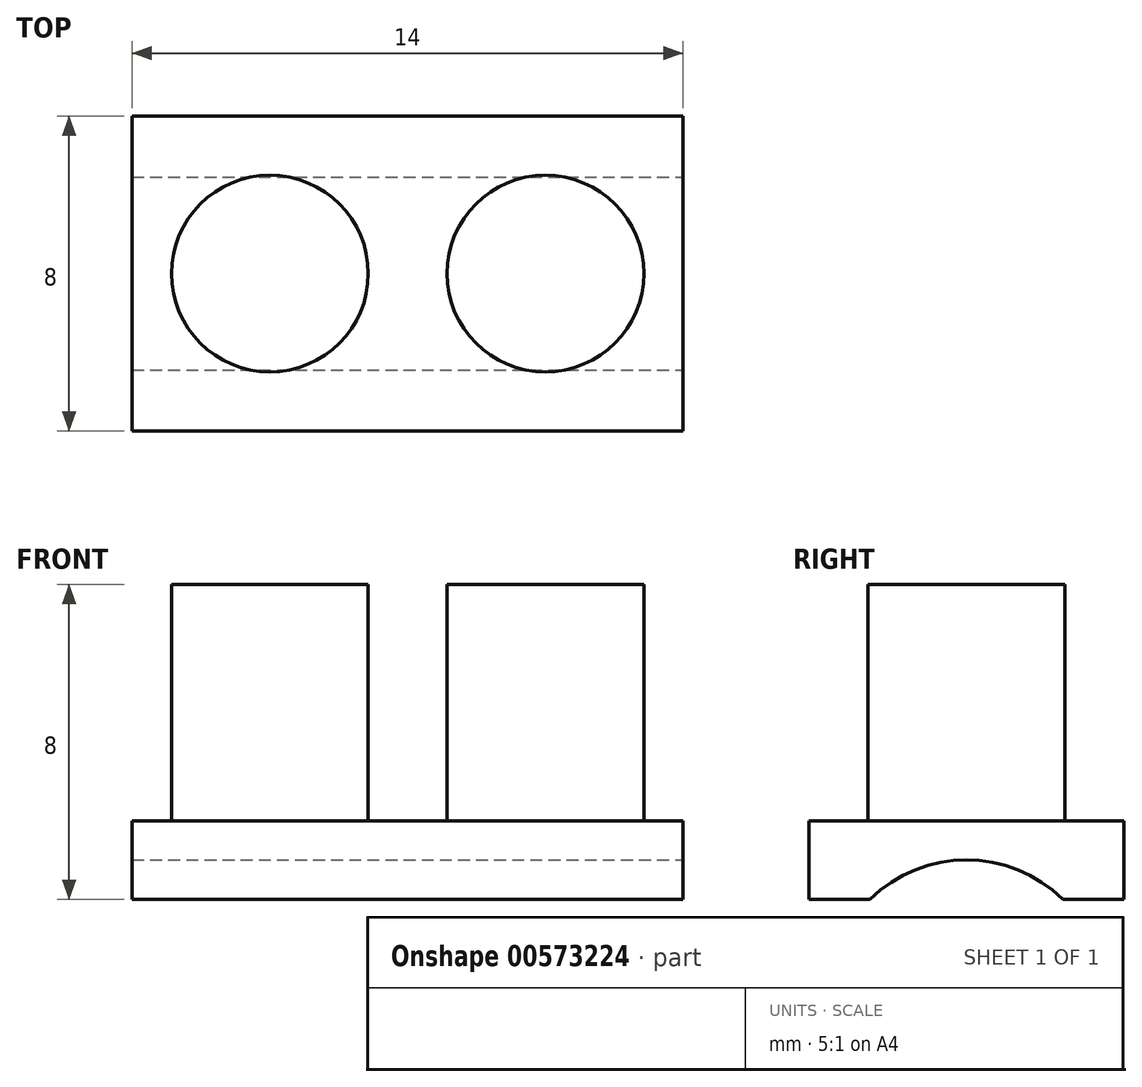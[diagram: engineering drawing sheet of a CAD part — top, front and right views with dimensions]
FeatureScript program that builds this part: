
annotation { "Feature Type Name" : "Feature", "Feature Type Description" : "" }
export const myFeature = defineFeature(function(context is Context, id is Id, definition is map)
    precondition{}
    {
        {
            var Q0;
            Q0=qCreatedBy(makeId("Front.planeOp"),FACE);
            var sketch = newSketch(context, id + "F0", { "sketchPlane" : qUnion([Q0])});
            skLineSegment(sketch, "E0.bottom", {"start": v(-1.14, 0) * mm, "end": v(12.86, 0) * mm});
            skLineSegment(sketch, "E0.top", {"start": v(-1.14, 2) * mm, "end": v(12.86, 2) * mm});
            skLineSegment(sketch, "E0.left", {"start": v(-1.14, 0) * mm, "end": v(-1.14, 2) * mm});
            skLineSegment(sketch, "E0.right", {"start": v(12.86, 0) * mm, "end": v(12.86, 2) * mm});
            skSolve(sketch);
        }
        {
            var Q0;
            Q0=makeQuery(id+"F0.imprint","IMPRINT",FACE,{"disambiguationData":[TD([[makeQuery(id+"F0.imprint","IMPRINT",EDGE,{"derivedFrom":sQuery(id+"F0.wireOp",EDGE,"E0.bottom")}),1.0]])]});
            extrude(context, id + "F1", {"entities" : qUnion([Q0]), "endBound" : BoundingType.SYMMETRIC, "depth" : 8 * mm, "offsetDistance" : 25.4 * mm});
        }
        {
            var Q0;
            Q0=makeQuery(id+"F1.opExtrude","SWEPT_FACE",FACE,{"disambiguationData":[OSD([sQuery(id+"F0.wireOp",EDGE,"E0.top")])]});
            var sketch = newSketch(context, id + "F2", { "sketchPlane" : qUnion([Q0])});
            skCircle(sketch, "E1", {"center": v(2.36, 0) * mm, "radius": 2.5 * mm});
            skCircle(sketch, "E2", {"center": v(9.36, 0) * mm, "radius": 2.5 * mm});
            skSolve(sketch);
        }
        {
            var Q0;
            Q0=makeQuery(id+"F2.imprint","IMPRINT",FACE,{"disambiguationData":[TD([[makeQuery(id+"F2.imprint","IMPRINT",EDGE,{"derivedFrom":sQuery(id+"F2.wireOp",EDGE,"E2")}),1.0]])]});
            var Q1;
            Q1=makeQuery(id+"F2.imprint","IMPRINT",FACE,{"disambiguationData":[TD([[makeQuery(id+"F2.imprint","IMPRINT",EDGE,{"derivedFrom":sQuery(id+"F2.wireOp",EDGE,"E1")}),1.0]])]});
            extrude(context, id + "F3", {"entities" : qUnion([Q0, Q1]), "operationType" : NewBodyOperationType.ADD, "depth" : 6 * mm, "offsetDistance" : 25.4 * mm});
        }
        {
            var Q0;
            Q0=makeQuery(id+"F1.opExtrude","SWEPT_FACE",FACE,{"disambiguationData":[OSD([sQuery(id+"F0.wireOp",EDGE,"E0.left")])]});
            var Q1;
            Q1=makeQuery(id+"F1.opExtrude","SWEPT_FACE",FACE,{"disambiguationData":[OSD([sQuery(id+"F0.wireOp",EDGE,"E0.right")])]});
            cPlane(context, id + "F4", {"entities" : qUnion([Q0, Q1]), "cplaneType" : CPlaneType.MID_PLANE, "offset" : 25.4 * mm, "width" : 152.4 * mm, "height" : 152.4 * mm});
        }
        {
            var Q0;
            Q0=qCreatedBy(id+"F4.planeOp",FACE);
            var sketch = newSketch(context, id + "F5", { "sketchPlane" : qUnion([Q0])});
            skCircle(sketch, "E3", {"center": v(0, -2.5) * mm, "radius": 3.5 * mm});
            skSolve(sketch);
        }
        {
            var Q0;
            Q0=makeQuery(id+"F5.imprint","IMPRINT",FACE,{"disambiguationData":[TD([[makeQuery(id+"F5.imprint","IMPRINT",EDGE,{"derivedFrom":sQuery(id+"F5.wireOp",EDGE,"E3")}),1.0]])]});
            extrude(context, id + "F6", {"entities" : qUnion([Q0]), "operationType" : NewBodyOperationType.REMOVE, "endBound" : BoundingType.SYMMETRIC, "depth" : 25.4 * mm, "offsetDistance" : 25.4 * mm});
        }
    });
